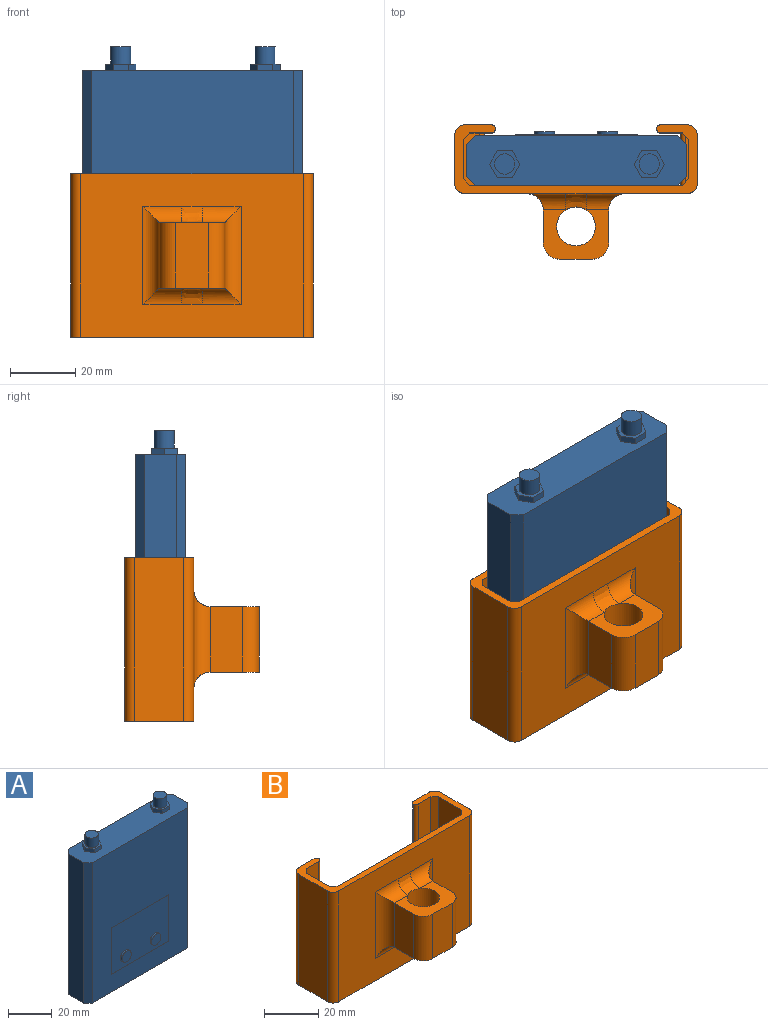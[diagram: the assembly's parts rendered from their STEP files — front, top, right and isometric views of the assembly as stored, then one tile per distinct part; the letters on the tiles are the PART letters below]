
ASSEMBLY  parts=2 mates=1
PART A: 45 faces, bbox 67.2x16.4x86 mm
  f0: plane 78.7x61.73mm, normal (0,-1,0), area 3890.2mm2, adj f1,f5,f32,f33,f34,f35,f41,f44
  f1: plane 67.23x15.31mm, normal (0,0,1), area 903.3mm2, adj f0,f2,f3,f4,f14,f15,f16,f17
  f2: plane 78.7x9.81mm, normal (-1,0,0), area 772mm2, adj f1,f5,f41,f42
  f3: plane 78.7x9.81mm, normal (1,0,0), area 772mm2, adj f1,f5,f43,f44
  f4: plane 78.7x61.73mm, normal (0,1,0), area 4858.2mm2, adj f1,f5,f42,f43
  f5: plane 67.23x15.31mm, normal (0,0,-1), area 975.7mm2, adj f0,f2,f3,f4,f6,f8,f10,f12
  f6: cylinder r=1.75mm len=25mm, axis (0,0,-1), area 274.9mm2, adj f5,f7
  f7: plane 3.5x3.5mm, normal (0,0,-1), area 9.6mm2, adj f6
  f8: cylinder r=1.75mm len=25mm, axis (0,0,-1), area 274.9mm2, adj f5,f9
  f9: plane 3.5x3.5mm, normal (0,0,-1), area 9.6mm2, adj f8
  f10: cylinder r=1.75mm len=25mm, axis (0,0,-1), area 274.9mm2, adj f5,f11
  f11: plane 3.5x3.5mm, normal (0,0,-1), area 9.6mm2, adj f10
  f12: cylinder r=1.75mm len=25mm, axis (0,0,-1), area 274.9mm2, adj f5,f13
  f13: plane 3.5x3.5mm, normal (0,0,-1), area 9.6mm2, adj f12
  f14: plane 4x2.31mm, normal (-0.87,0.5,0), area 9.2mm2, adj f1,f15,f19,f20
  f15: plane 4x2.31mm, normal (-0.87,-0.5,0), area 9.2mm2, adj f1,f14,f16,f20
  f16: plane 4.62x2mm, normal (0,-1,0), area 9.2mm2, adj f1,f15,f17,f20
  f17: plane 4x2.31mm, normal (0.87,-0.5,0), area 9.2mm2, adj f1,f16,f18,f20
  f18: plane 4x2.31mm, normal (0.87,0.5,0), area 9.2mm2, adj f1,f17,f19,f20
  f19: plane 4.62x2mm, normal (0,1,0), area 9.2mm2, adj f1,f14,f18,f20
  f20: plane 9.24x8mm, normal (0,0,1), area 25.2mm2, adj f14,f15,f16,f17,f18,f19,f30
  f21: plane 4x2.31mm, normal (-0.87,0.5,0), area 9.2mm2, adj f1,f22,f26,f27
  f22: plane 4x2.31mm, normal (-0.87,-0.5,0), area 9.2mm2, adj f1,f21,f23,f27
  f23: plane 4.62x2mm, normal (0,-1,0), area 9.2mm2, adj f1,f22,f24,f27
  f24: plane 4x2.31mm, normal (0.87,-0.5,0), area 9.2mm2, adj f1,f23,f25,f27
  f25: plane 4x2.31mm, normal (0.87,0.5,0), area 9.2mm2, adj f1,f24,f26,f27
  f26: plane 4.62x2mm, normal (0,1,0), area 9.2mm2, adj f1,f21,f25,f27
  f27: plane 9.24x8mm, normal (0,0,1), area 25.2mm2, adj f21,f22,f23,f24,f25,f26,f28
  f28: cylinder r=3.1mm len=6.2mm, axis (0,0,-1), area 102.8mm2, adj f27,f29
  f29: plane 6.2x6.2mm, normal (0,0,1), area 30.2mm2, adj f28
  f30: cylinder r=3.1mm len=6.2mm, axis (0,0,-1), area 102.8mm2, adj f20,f31
  f31: plane 6.2x6.2mm, normal (0,0,1), area 30.2mm2, adj f30
  f32: plane 26x0.1mm, normal (-1,0,0), area 2.6mm2, adj f0,f33,f35,f36
  f33: plane 37.23x0.1mm, normal (0,0,-1), area 3.7mm2, adj f0,f32,f34,f36
  f34: plane 26x0.1mm, normal (1,0,0), area 2.6mm2, adj f0,f33,f35,f36
  f35: plane 37.23x0.1mm, normal (0,0,1), area 3.7mm2, adj f0,f32,f34,f36
  f36: plane 37.23x26mm, normal (0,-1,0), area 911.4mm2, adj f32,f33,f34,f35,f37,f39
  f37: cylinder r=3mm len=6mm, axis (0,1,0), area 18.8mm2, adj f36,f38
  f38: plane 6x6mm, normal (0,-1,0), area 28.3mm2, adj f37
  f39: cylinder r=3mm len=6mm, axis (0,1,0), area 18.8mm2, adj f36,f40
  f40: plane 6x6mm, normal (0,-1,0), area 28.3mm2, adj f39
  f41: plane 78.7x2.75mm, normal (-0.71,-0.71,0), area 306.1mm2, adj f0,f1,f2,f5
  f42: plane 78.7x2.75mm, normal (-0.71,0.71,0), area 306.1mm2, adj f1,f2,f4,f5
  f43: plane 78.7x2.75mm, normal (0.71,0.71,0), area 306.1mm2, adj f1,f3,f4,f5
  f44: plane 78.7x2.75mm, normal (0.71,-0.71,0), area 306.1mm2, adj f0,f1,f3,f5
PART B: 46 faces, bbox 74.1x41.1x50.1 mm
  f0: plane 50x7.5mm, normal (0,-1,0), area 324.6mm2, adj f10,f11,f16,f24,f25,f28
  f1: plane 47.5x12mm, normal (-1,0,0), area 570mm2, adj f10,f13,f16,f17
  f2: plane 66x50mm, normal (0,1,0), area 3239.3mm2, adj f10,f11,f12,f15,f17,f22,f23,f24
  f3: plane 47.5x12mm, normal (1,0,0), area 570mm2, adj f10,f12,f14,f15
  f4: plane 50x6.5mm, normal (0,-1,0), area 314.7mm2, adj f10,f11,f12,f14,f22,f23,f27
  f5: plane 50x8mm, normal (0,1,0), area 400mm2, adj f10,f11,f18,f26
  f6: plane 50x15mm, normal (-1,0,0), area 750mm2, adj f10,f11,f18,f19
  f7: plane 68x50mm, normal (0,-1,0), area 2500.6mm2, adj f10,f11,f19,f20,f36,f37,f38,f39
  f8: plane 50x15mm, normal (1,0,0), area 750mm2, adj f10,f11,f20,f21
  f9: plane 50x8mm, normal (0,1,0), area 400mm2, adj f10,f11,f21,f29
  f10: plane 74x21mm, normal (0,0,1), area 325.8mm2, adj f0,f1,f2,f3,f4,f5,f6,f7
  f11: plane 74x21mm, normal (0,0,-1), area 413.8mm2, adj f0,f2,f4,f5,f6,f7,f8,f9
  f12: plane 16x5mm, normal (0,0,1), area 76mm2, adj f2,f3,f4,f14,f15,f22
  f13: plane 14x1mm, normal (0,0,1), area 13mm2, adj f1,f16,f17,f24
  f14: plane 47.5x2mm, normal (0.71,-0.71,0), area 134.4mm2, adj f3,f4,f10,f12
  f15: plane 47.5x2mm, normal (0.71,0.71,0), area 134.4mm2, adj f2,f3,f10,f12
  f16: plane 47.95x2.07mm, normal (-0.71,-0.71,0), area 134.5mm2, adj f0,f1,f10,f13,f24
  f17: plane 47.95x2.07mm, normal (-0.71,0.71,0), area 134.5mm2, adj f1,f2,f10,f13,f24
  f18: cylinder r=3mm len=50mm, axis (0,0,-1), area 235.6mm2, adj f5,f6,f10,f11
  f19: cylinder r=3mm len=50mm, axis (0,0,-1), area 235.6mm2, adj f6,f7,f10,f11
  f20: cylinder r=3mm len=50mm, axis (0,0,-1), area 235.6mm2, adj f7,f8,f10,f11
  f21: cylinder r=3mm len=50mm, axis (0,0,-1), area 235.6mm2, adj f8,f9,f10,f11
  f22: cylinder r=1.5mm len=16mm, axis (0,-1,0), area 33.7mm2, adj f2,f4,f12,f23
  f23: cylinder r=1.5mm len=16mm, axis (0,1,0), area 33.7mm2, adj f2,f4,f11,f22
  f24: cylinder r=1.5mm len=16mm, axis (0,1,0), area 32.6mm2, adj f0,f2,f13,f16,f17,f25
  f25: cylinder r=1.5mm len=16mm, axis (0,-1,0), area 33.7mm2, adj f0,f2,f11,f24
  f26: cylinder r=1.5mm len=50mm, axis (0,0,-1), area 105.3mm2, adj f5,f10,f11,f27
  f27: cylinder r=1.5mm len=50mm, axis (0,0,-1), area 105.3mm2, adj f4,f10,f11,f26
  f28: cylinder r=1.5mm len=50mm, axis (0,0,-1), area 105.3mm2, adj f0,f10,f11,f29
  f29: cylinder r=1.5mm len=50mm, axis (0,0,-1), area 105.3mm2, adj f9,f10,f11,f28
  f30: plane 20x15mm, normal (0,0,-1), area 182.7mm2, adj f31,f33,f34,f35,f36,f39,f44,f45
  f31: plane 20x10mm, normal (1,0,0), area 200mm2, adj f30,f32,f41,f44
  f32: plane 20x15mm, normal (0,0,1), area 182.7mm2, adj f31,f33,f34,f35,f40,f43,f44,f45
  f33: plane 20x10mm, normal (-1,0,0), area 200mm2, adj f30,f32,f38,f45
  f34: plane 20x10mm, normal (0,-1,0), area 200mm2, adj f30,f32,f44,f45
  f35: cylinder r=5.93mm len=20mm, axis (0,0,-1), area 745.5mm2, adj f30,f32,f37,f42
  f36: cylinder r=5mm len=11.81mm, axis (1,0,0), area 67.7mm2, adj f7,f30,f37,f38
  f37: bspline ~6.39x5mm, area 46.1mm2, adj f7,f35,f36,f39
  f38: cylinder r=5mm len=30mm, axis (0,0,-1), area 185.6mm2, adj f7,f33,f36,f40
  f39: cylinder r=5mm len=11.81mm, axis (1,0,0), area 67.7mm2, adj f7,f30,f37,f41
  f40: cylinder r=5mm len=11.81mm, axis (-1,0,0), area 67.7mm2, adj f7,f32,f38,f42
  f41: cylinder r=5mm len=30mm, axis (0,0,1), area 185.6mm2, adj f7,f31,f39,f43
  f42: bspline ~6.39x5mm, area 46.1mm2, adj f7,f35,f40,f43
  f43: cylinder r=5mm len=11.81mm, axis (-1,0,0), area 67.7mm2, adj f7,f32,f41,f42
  f44: cylinder r=5mm len=20mm, axis (0,0,-1), area 157.1mm2, adj f30,f31,f32,f34
  f45: cylinder r=5mm len=20mm, axis (0,0,1), area 157.1mm2, adj f30,f32,f33,f34
PLACE A rot(axis=(0,0,1),180deg) t=(59.05,48.91,3.67)mm
PLACE B t=(44.6,42.27,0.94)mm
MATE fastened A.f4 <-> B.f2  axis (0,-1,0) through (57.29,42.27,43.02)mm
